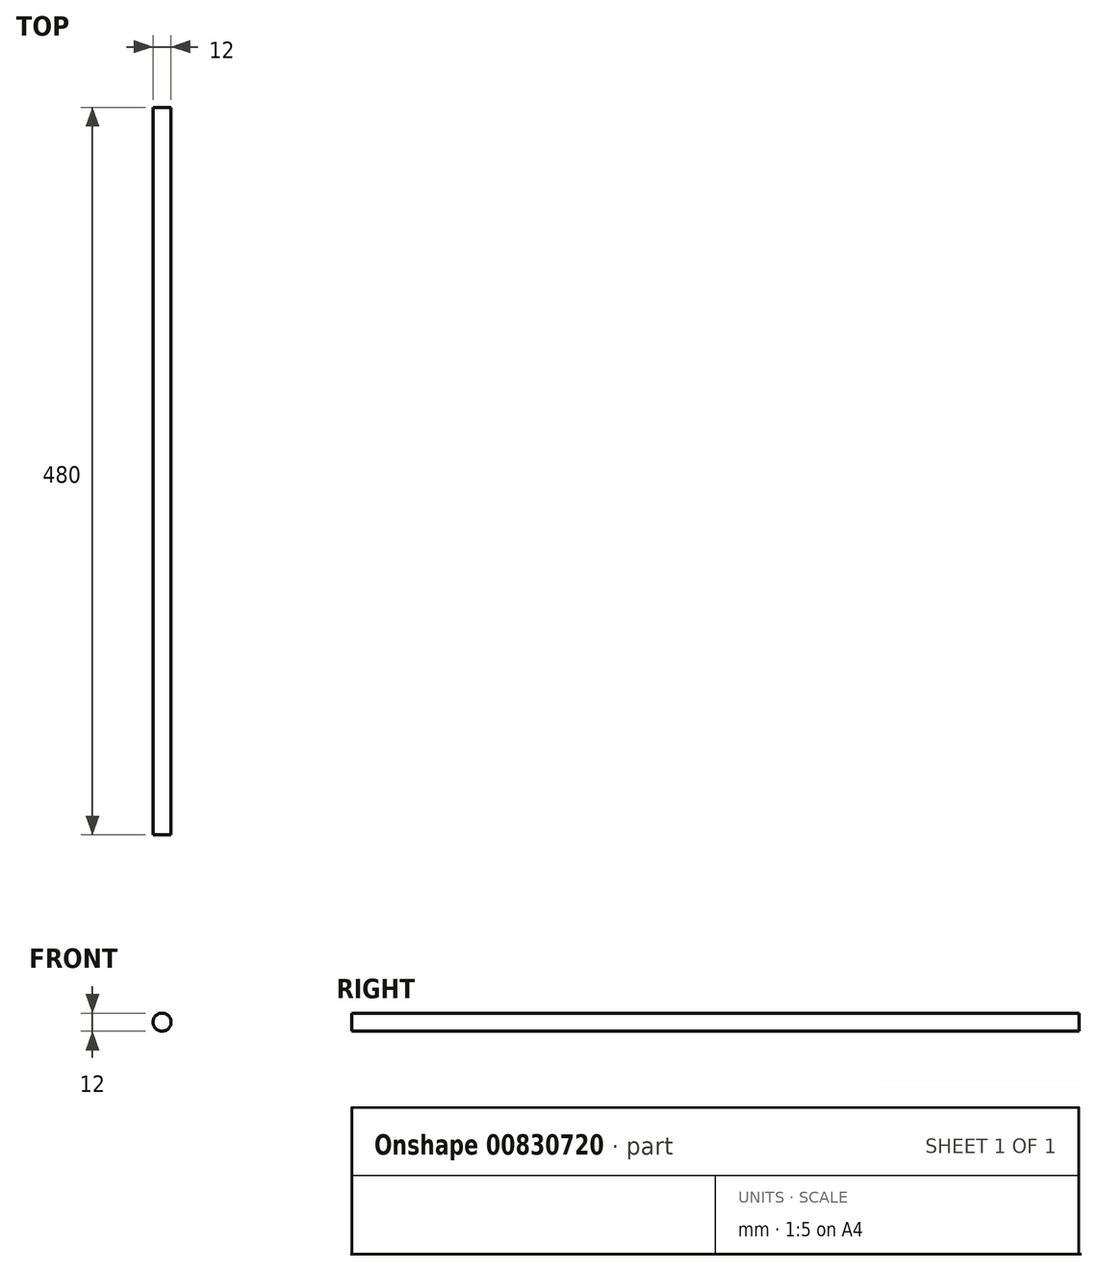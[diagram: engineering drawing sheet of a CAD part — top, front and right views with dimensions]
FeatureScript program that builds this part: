
annotation { "Feature Type Name" : "Feature", "Feature Type Description" : "" }
export const myFeature = defineFeature(function(context is Context, id is Id, definition is map)
    precondition{}
    {
        {
            assignVariable(context, id + "F0", {"name" : "RodLength", "anyValue" : 480});
        }
        {
            var Q0;
            Q0=qCreatedBy(makeId("Front.planeOp"),FACE);
            var sketch = newSketch(context, id + "F1", { "sketchPlane" : qUnion([Q0])});
            skCircle(sketch, "E0", {"center": v(0, 0) * mm, "radius": 6 * mm});
            skSolve(sketch);
        }
        {
            var Q0;
            Q0=makeQuery(id+"F1.imprint","IMPRINT",FACE,{"disambiguationData":[TD([[makeQuery(id+"F1.imprint","IMPRINT",EDGE,{"derivedFrom":sQuery(id+"F1.wireOp",EDGE,"E0")}),1.0]])]});
            extrude(context, id + "F2", {"entities" : qUnion([Q0]), "endBound" : BoundingType.SYMMETRIC, "depth" : (getVariable(context, 'RodLength')) * mm, "offsetDistance" : 25 * mm});
        }
        {
            var Q0;
            Q0=makeQuery(id+"F2.opExtrude","SWEPT_BODY",BODY,{"disambiguationData":[OSD([sQuery(id+"F1.wireOp",EDGE,"E0")])]});
            transform(context, id + "F3", {"entities" : qUnion([Q0]), "transformType" : TransformType.TRANSLATION_3D, "dx" : 0 * mm, "dy" : 0 * mm, "dz" : 0 * mm, "makeCopy" : true});
        }
        {
            var Q0;
            Q0=makeQuery(id+"F3.opPattern","COPY",BODY,{"derivedFrom":makeQuery(id+"F2.opExtrude","SWEPT_BODY",BODY,{"disambiguationData":[OSD([sQuery(id+"F1.wireOp",EDGE,"E0")])]}),"instanceName":"1"});
            deleteBodies(context, id + "F4", {"entities" : qUnion([Q0])});
        }
    });
